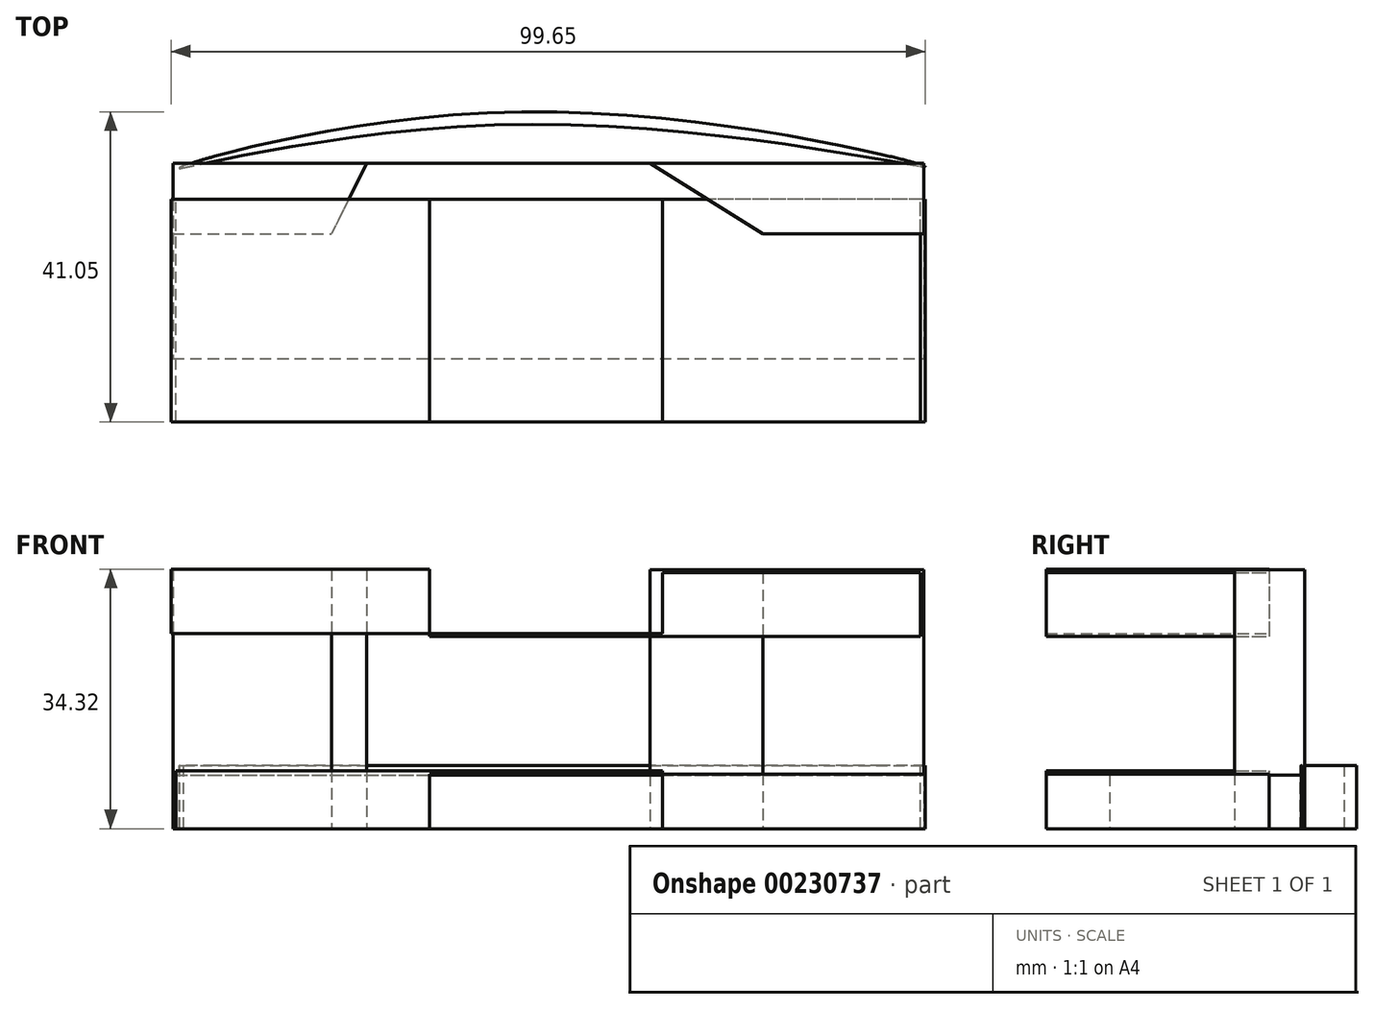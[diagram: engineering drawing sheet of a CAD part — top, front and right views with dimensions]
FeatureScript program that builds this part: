
annotation { "Feature Type Name" : "Feature", "Feature Type Description" : "" }
export const myFeature = defineFeature(function(context is Context, id is Id, definition is map)
    precondition{}
    {
        {
            var Q0;
            Q0=qCreatedBy(makeId("Top.planeOp"),FACE);
            var sketch = newSketch(context, id + "F0", { "sketchPlane" : qUnion([Q0])});
            skLineSegment(sketch, "E0.bottom", {"start": v(-46.1, 4.76) * mm, "end": v(53.14, 4.76) * mm});
            skLineSegment(sketch, "E0.top", {"start": v(-46.1, -4.55) * mm, "end": v(53.14, -4.55) * mm});
            skLineSegment(sketch, "E0.left", {"start": v(-46.1, 4.76) * mm, "end": v(-46.1, -4.55) * mm});
            skLineSegment(sketch, "E0.right", {"start": v(53.14, 4.76) * mm, "end": v(53.14, -4.55) * mm});
            skLineSegment(sketch, "E1", {"start": v(53.14, -4.55) * mm, "end": v(53.14, -20.88) * mm});
            skLineSegment(sketch, "E2", {"start": v(-25.12, -4.55) * mm, "end": v(-25.12, -21.08) * mm});
            skLineSegment(sketch, "E3", {"start": v(-0.1, -4.55) * mm, "end": v(-0.1, -21.08) * mm});
            skLineSegment(sketch, "E4", {"start": v(-25.12, -21.08) * mm, "end": v(53.14, -21.08) * mm});
            skLineSegment(sketch, "E5", {"start": v(31.88, -4.55) * mm, "end": v(31.88, -21.08) * mm});
            skLineSegment(sketch, "E6.bottom", {"start": v(-46.1, -4.55) * mm, "end": v(-25.12, -4.55) * mm});
            skLineSegment(sketch, "E6.top", {"start": v(-46.1, -21.08) * mm, "end": v(-25.12, -21.08) * mm});
            skLineSegment(sketch, "E6.left", {"start": v(-46.1, -4.55) * mm, "end": v(-46.1, -21.08) * mm});
            skLineSegment(sketch, "E7.bottom", {"start": v(-25.12, -21.08) * mm, "end": v(-0.1, -21.08) * mm});
            skLineSegment(sketch, "E7.top", {"start": v(-25.12, -4.55) * mm, "end": v(-0.1, -4.55) * mm});
            skLineSegment(sketch, "E7.left", {"start": v(-25.12, -21.08) * mm, "end": v(-25.12, -4.55) * mm});
            skLineSegment(sketch, "E7.right", {"start": v(-0.1, -21.08) * mm, "end": v(-0.1, -4.55) * mm});
            skLineSegment(sketch, "E8.bottom", {"start": v(-0.1, -21.08) * mm, "end": v(31.88, -21.08) * mm});
            skLineSegment(sketch, "E8.top", {"start": v(-0.1, -4.55) * mm, "end": v(31.88, -4.55) * mm});
            skLineSegment(sketch, "E8.right", {"start": v(31.88, -21.08) * mm, "end": v(31.88, -4.55) * mm});
            skLineSegment(sketch, "E9.bottom", {"start": v(31.88, -21.08) * mm, "end": v(53.14, -21.08) * mm});
            skLineSegment(sketch, "E9.top", {"start": v(31.88, -4.55) * mm, "end": v(53.14, -4.55) * mm});
            skLineSegment(sketch, "E9.right", {"start": v(53.14, -21.08) * mm, "end": v(53.14, -4.55) * mm});
            skLineSegment(sketch, "E10", {"start": v(-20.47, 4.76) * mm, "end": v(-25.12, -4.55) * mm});
            skLineSegment(sketch, "E11", {"start": v(16.95, 4.76) * mm, "end": v(31.88, -4.55) * mm});
            skSolve(sketch);
        }
        {
            var Q0;
            Q0=qCreatedBy(makeId("Top.planeOp"),FACE);
            var sketch = newSketch(context, id + "F1", { "sketchPlane" : qUnion([Q0])});
            skLineSegment(sketch, "E12", {"start": v(34.32, -21.7) * mm, "end": v(52.93, -46.52) * mm});
            skLineSegment(sketch, "E13", {"start": v(-32.46, -21.5) * mm, "end": v(-46.31, -45.7) * mm});
            skFitSpline(sketch, "E14", {"points": [v(-32.46, -21.5) * mm, v(0, -36.39) * mm, v(34.32, -21.7) * mm], "startDerivative": vector(63.53, -44.81) * mm, "endDerivative": vector(68.35, 43.91) * mm});
            skFitSpline(sketch, "E15", {"points": [v(-45.28, 4.13) * mm, v(0, 9.92) * mm, v(53.34, 4.34) * mm, v(0, 11.58) * mm, v(-45.28, 4.13) * mm]});
            skLineSegment(sketch, "E16", {"start": v(-46.31, -21.7) * mm, "end": v(-46.31, -45.7) * mm});
            skLineSegment(sketch, "E17", {"start": v(52.93, -21.5) * mm, "end": v(52.93, -46.52) * mm});
            skLineSegment(sketch, "E18", {"start": v(-46.31, -21.7) * mm, "end": v(-45.28, 4.13) * mm});
            skFitSpline(sketch, "E19", {"points": [v(-45.28, 4.13) * mm, v(0, 14.68) * mm, v(53.34, 4.34) * mm, v(0, 18.4) * mm, v(-45.28, 4.13) * mm]});
            skSolve(sketch);
        }
        {
            var Q0;
            {var subQ0=sQuery(id+"F1.wireOp",EDGE,"E19");var subQ1=sQuery(id+"F1.wireOp",EDGE,"E15");var subQ2=makeQuery(id+"F1.imprint","INTERSECT",VERTEX,{"disambiguationData":[OD(0.0)],"derivedFrom":[subQ1,subQ0]});Q0=makeQuery(id+"F1.imprint","IMPRINT",FACE,{"disambiguationData":[TD([[makeQuery(id+"F1.imprint","IMPRINT",EDGE,{"disambiguationData":[TD([[subQ2,-1.0]])],"derivedFrom":subQ1}),1.0]])]});}
            var Q1;
            {var subQ0=sQuery(id+"F1.wireOp",EDGE,"E19");var subQ1=sQuery(id+"F1.wireOp",EDGE,"E15");var subQ2=makeQuery(id+"F1.imprint","INTERSECT",VERTEX,{"disambiguationData":[OD(1.0)],"derivedFrom":[subQ1,subQ0]});Q1=makeQuery(id+"F1.imprint","IMPRINT",FACE,{"disambiguationData":[TD([[makeQuery(id+"F1.imprint","IMPRINT",EDGE,{"disambiguationData":[TD([[subQ2,-1.0]])],"derivedFrom":subQ1}),-1.0]])]});}
            var Q2;
            {var subQ0=sQuery(id+"F1.wireOp",EDGE,"E19");var subQ1=sQuery(id+"F1.wireOp",EDGE,"E15");var subQ2=makeQuery(id+"F1.imprint","INTERSECT",VERTEX,{"disambiguationData":[OD(3.0)],"derivedFrom":[subQ1,subQ0]});Q2=makeQuery(id+"F1.imprint","IMPRINT",FACE,{"disambiguationData":[TD([[makeQuery(id+"F1.imprint","IMPRINT",EDGE,{"disambiguationData":[TD([[subQ2,-1.0]])],"derivedFrom":subQ1}),-1.0]])]});}
            var Q3;
            {var subQ0=sQuery(id+"F1.wireOp",EDGE,"E19");var subQ1=sQuery(id+"F1.wireOp",EDGE,"E15");var subQ2=makeQuery(id+"F1.imprint","INTERSECT",VERTEX,{"disambiguationData":[OD(2.0)],"derivedFrom":[subQ1,subQ0]});Q3=makeQuery(id+"F1.imprint","IMPRINT",FACE,{"disambiguationData":[TD([[makeQuery(id+"F1.imprint","IMPRINT",EDGE,{"disambiguationData":[TD([[subQ2,-1.0]])],"derivedFrom":subQ1}),1.0]])]});}
            var Q4;
            {var subQ0=sQuery(id+"F1.wireOp",EDGE,"E19");var subQ1=sQuery(id+"F1.wireOp",EDGE,"E15");var subQ2=makeQuery(id+"F1.imprint","INTERSECT",VERTEX,{"disambiguationData":[OD(3.0)],"derivedFrom":[subQ1,subQ0]});Q4=makeQuery(id+"F1.imprint","IMPRINT",FACE,{"disambiguationData":[TD([[makeQuery(id+"F1.imprint","IMPRINT",EDGE,{"disambiguationData":[TD([[subQ2,-1.0]])],"derivedFrom":subQ1}),1.0]])]});}
            var Q5;
            {var subQ0=sQuery(id+"F1.wireOp",EDGE,"E19");var subQ1=sQuery(id+"F1.wireOp",EDGE,"E15");var subQ2=makeQuery(id+"F1.imprint","INTERSECT",VERTEX,{"disambiguationData":[OD(4.0)],"derivedFrom":[subQ1,subQ0]});Q5=makeQuery(id+"F1.imprint","IMPRINT",FACE,{"disambiguationData":[TD([[makeQuery(id+"F1.imprint","IMPRINT",EDGE,{"disambiguationData":[TD([[subQ2,-1.0]])],"derivedFrom":subQ1}),-1.0]])]});}
            var Q6;
            {var subQ0=sQuery(id+"F1.wireOp",EDGE,"E19");var subQ1=sQuery(id+"F1.wireOp",EDGE,"E15");var subQ2=makeQuery(id+"F1.imprint","INTERSECT",VERTEX,{"disambiguationData":[OD(1.0)],"derivedFrom":[subQ1,subQ0]});Q6=makeQuery(id+"F1.imprint","IMPRINT",FACE,{"disambiguationData":[TD([[makeQuery(id+"F1.imprint","IMPRINT",EDGE,{"disambiguationData":[TD([[subQ2,-1.0]])],"derivedFrom":subQ1}),1.0]])]});}
            extrude(context, id + "F2", {"entities" : qUnion([Q0, Q1, Q2, Q3, Q4, Q5, Q6]), "depth" : 8.38 * mm});
        }
        {
            var Q0;
            Q0=makeQuery(id+"F0.imprint","IMPRINT",FACE,{"disambiguationData":[TD([[makeQuery(id+"F0.imprint","IMPRINT",EDGE,{"derivedFrom":sQuery(id+"F0.wireOp",EDGE,"E7.bottom")}),1.0]])]});
            var Q1;
            Q1=makeQuery(id+"F0.imprint","IMPRINT",FACE,{"disambiguationData":[TD([[makeQuery(id+"F0.imprint","IMPRINT",EDGE,{"derivedFrom":sQuery(id+"F0.wireOp",EDGE,"E8.bottom")}),1.0]])]});
            var Q2;
            {var subQ0=sQuery(id+"F0.wireOp",EDGE,"E9.bottom");Q2=makeQuery(id+"F0.imprint","IMPRINT",FACE,{"disambiguationData":[TD([[makeQuery(id+"F0.imprint","IMPRINT",EDGE,{"derivedFrom":subQ0}),1.0]])]});}
            var Q3;
            Q3=makeQuery(id+"F0.imprint","IMPRINT",FACE,{"disambiguationData":[TD([[makeQuery(id+"F0.imprint","IMPRINT",EDGE,{"derivedFrom":sQuery(id+"F0.wireOp",EDGE,"E6.bottom")}),-1.0]])]});
            var Q4;
            {var subQ0=sQuery(id+"F0.wireOp",EDGE,"E0.left");Q4=makeQuery(id+"F0.imprint","IMPRINT",FACE,{"disambiguationData":[TD([[makeQuery(id+"F0.imprint","IMPRINT",EDGE,{"derivedFrom":subQ0}),1.0]])]});}
            var Q5;
            {var subQ0=sQuery(id+"F0.wireOp",EDGE,"E0.right");Q5=makeQuery(id+"F0.imprint","IMPRINT",FACE,{"disambiguationData":[TD([[makeQuery(id+"F0.imprint","IMPRINT",EDGE,{"derivedFrom":subQ0}),-1.0]])]});}
            extrude(context, id + "F3", {"entities" : qUnion([Q0, Q1, Q2, Q3, Q4, Q5]), "depth" : 34.3 * mm});
        }
        {
            var Q0;
            Q0 = qSketchRegion(id + "F0", true);
            extrude(context, id + "F4", {"entities" : qUnion([Q0]), "depth" : 7.11 * mm});
        }
        {
            var Q0;
            Q0=qCreatedBy(makeId("Front.planeOp"),FACE);
            var sketch = newSketch(context, id + "F5", { "sketchPlane" : qUnion([Q0])});
            skLineSegment(sketch, "E20.bottom", {"start": v(-46.31, 34.32) * mm, "end": v(-12.2, 34.32) * mm});
            skLineSegment(sketch, "E20.top", {"start": v(-46.31, 25.84) * mm, "end": v(-12.2, 25.84) * mm});
            skLineSegment(sketch, "E20.left", {"start": v(-46.31, 34.32) * mm, "end": v(-46.31, 25.84) * mm});
            skLineSegment(sketch, "E20.right", {"start": v(-12.2, 34.32) * mm, "end": v(-12.2, 25.84) * mm});
            skLineSegment(sketch, "E21.bottom", {"start": v(52.72, 33.9) * mm, "end": v(18.6, 33.9) * mm});
            skLineSegment(sketch, "E21.top", {"start": v(52.72, 25.43) * mm, "end": v(18.6, 25.43) * mm});
            skLineSegment(sketch, "E21.left", {"start": v(52.72, 33.9) * mm, "end": v(52.72, 25.43) * mm});
            skLineSegment(sketch, "E21.right", {"start": v(18.6, 33.9) * mm, "end": v(18.6, 25.43) * mm});
            skLineSegment(sketch, "E22.bottom", {"start": v(-12.2, 25.84) * mm, "end": v(18.6, 25.84) * mm});
            skLineSegment(sketch, "E22.top", {"start": v(-12.2, 25.43) * mm, "end": v(18.6, 25.43) * mm});
            skLineSegment(sketch, "E22.left", {"start": v(-12.2, 25.84) * mm, "end": v(-12.2, 25.43) * mm});
            skLineSegment(sketch, "E22.right", {"start": v(18.6, 25.84) * mm, "end": v(18.6, 25.43) * mm});
            skLineSegment(sketch, "E23.bottom", {"start": v(-45.7, 0) * mm, "end": v(-12.2, 0) * mm});
            skLineSegment(sketch, "E23.top", {"start": v(-45.7, 7.65) * mm, "end": v(-12.2, 7.65) * mm});
            skLineSegment(sketch, "E23.left", {"start": v(-45.7, 0) * mm, "end": v(-45.7, 7.65) * mm});
            skLineSegment(sketch, "E23.right", {"start": v(-12.2, 0) * mm, "end": v(-12.2, 7.65) * mm});
            skLineSegment(sketch, "E24.bottom", {"start": v(53.34, 0) * mm, "end": v(18.6, 0) * mm});
            skLineSegment(sketch, "E24.top", {"start": v(53.34, 7.24) * mm, "end": v(18.6, 7.24) * mm});
            skLineSegment(sketch, "E24.left", {"start": v(53.34, 0) * mm, "end": v(53.34, 7.24) * mm});
            skLineSegment(sketch, "E24.right", {"start": v(18.6, 0) * mm, "end": v(18.6, 7.24) * mm});
            skLineSegment(sketch, "E25.bottom", {"start": v(-12.2, 7.65) * mm, "end": v(18.6, 7.65) * mm});
            skLineSegment(sketch, "E25.top", {"start": v(-12.2, 7.24) * mm, "end": v(18.6, 7.24) * mm});
            skLineSegment(sketch, "E25.left", {"start": v(-12.2, 7.65) * mm, "end": v(-12.2, 7.24) * mm});
            skLineSegment(sketch, "E25.right", {"start": v(18.6, 7.65) * mm, "end": v(18.6, 7.24) * mm});
            skSolve(sketch);
        }
        {
            var Q0;
            Q0 = qSketchRegion(id + "F5", true);
            extrude(context, id + "F6", {"entities" : qUnion([Q0]), "depth" : 29.46 * mm});
        }
    });
